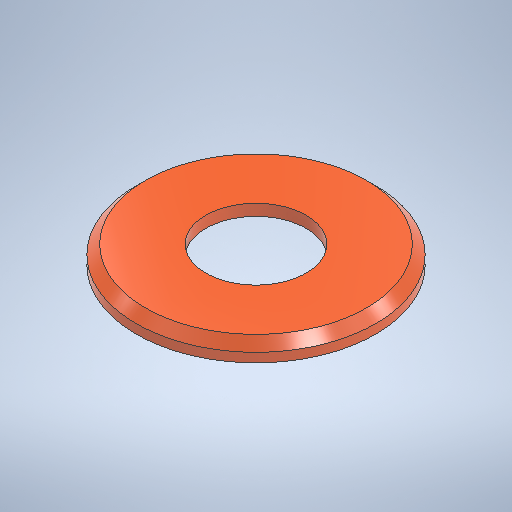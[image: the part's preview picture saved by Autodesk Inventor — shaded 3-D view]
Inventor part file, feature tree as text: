
AUTODESK INVENTOR PART (.ipt)
format: ipt  version: 2025 (Build 290162000, 162)  size: 310,272 bytes
history: native  units: in
note: dims shown in document units (in); Inventor stores cm internally (conversion verified against a paired STEP export)
features: extrude x7, sketch x7, chamfer x1
ambient origin geometry x8: Origin, YZ Plane, XZ Plane, XY Plane, X Axis, Y Axis, Z Axis, Center Point
bodies: Solid1 (feature_tree)
feature tree (15):
  extrude  "Extrusion1"  Depth=1.7323in
  extrude  "Extrusion2"  Depth=0.0197in
  extrude  "Extrusion3"  Depth=0.1575in
  extrude  "Extrusion4"  Depth=0.8661in
  extrude  "Extrusion5"  Depth=0.1575in
  extrude  "Extrusion6"  Depth=0.0787in TaperAngle=0.0deg
  extrude  "Extrusion7"  Depth=0.0394in TaperAngle=0.0deg
  chamfer  "Chamfer1"  Distance=0.0787in Angle=45.0deg
  sketch  "Sketch1"  dims[d0=1.9291in d1=1.7323in]
  sketch  "Sketch2"  dims[d2=0.0197in d3=0.0in d4=2.0669in]
  sketch  "Sketch3"  dims[d5=0.1575in d6=0.0in d7=1.378in]
  sketch  "Sketch4"  dims[d8=0.0984in d9=0.0in d10=0.8661in]
  sketch  "Sketch5"  dims[d11=0.1575in d12=0.0in d13=0.9843in]
  sketch  "Sketch6"  dims[d14=0.0394in d15=0.0in d16=0.0787in d17=0.0in]
  sketch  "Sketch7"  dims[d18=1.4567in d19=0.0394in d20=0.0in d21=0.0787in d22=0.0787in d23=45.0deg]
